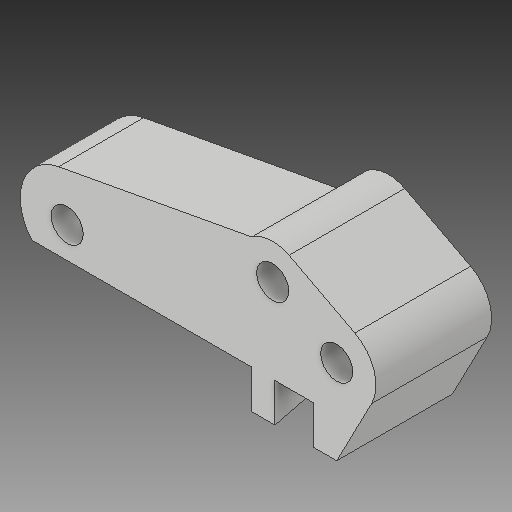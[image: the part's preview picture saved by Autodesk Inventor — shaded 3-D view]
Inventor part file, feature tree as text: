
AUTODESK INVENTOR PART (.ipt)
format: ipt  version: 2017 (Build 210142000, 142)  size: 423,936 bytes
history: native  units: mm
features: extrude x37, sketch x37, shell x1
ambient origin geometry x8: Origin, YZ Plane, XZ Plane, XY Plane, X Axis, Y Axis, Z Axis, Center Point
bodies: Solid1 (feature_tree)
feature tree (75):
  extrude  "Extrusion1"  Depth=37.0mm
  shell  "Shell1"  Thickness=20.0mm
  extrude  "Extrusion2"  Depth=11.0mm
  extrude  "Extrusion3"  TaperAngle=0.0deg  [1 undecoded]
  extrude  "Extrusion4"  Depth=5.0mm
  extrude  "Extrusion5"  TaperAngle=0.0deg  [1 undecoded]
  extrude  "Extrusion6"  Depth=10.0mm TaperAngle=0.0deg
  extrude  "Extrusion7"  Depth=15.0mm TaperAngle=0.0deg
  extrude  "Extrusion9"  Depth=8.5mm
  extrude  "Extrusion10"  Depth=15.0mm TaperAngle=0.0deg
  extrude  "Extrusion11"  Depth=35.46mm
  extrude  "Extrusion12"  Depth=15.0mm TaperAngle=0.0deg
  extrude  "Extrusion13"  Depth=4.5mm
  extrude  "Extrusion14"  Depth=15.0mm TaperAngle=0.0deg
  extrude  "Extrusion15"  Depth=8.5mm
  extrude  "Extrusion16"  Depth=15.0mm TaperAngle=0.0deg
  extrude  "Extrusion17"  Depth=28.505mm
  extrude  "Extrusion18"  Depth=15.0mm TaperAngle=0.0deg
  extrude  "Extrusion19"  Depth=36.0mm
  extrude  "Extrusion20"  Depth=15.0mm TaperAngle=0.0deg
  extrude  "Extrusion23"  Depth=5.0mm
  extrude  "Extrusion21"  Depth=4.1656mm
  extrude  "Extrusion22"  Depth=35.46mm
  extrude  "Extrusion24"  Depth=10.0mm
  extrude  "Extrusion25"  Depth=10.0mm TaperAngle=0.0deg
  extrude  "Extrusion26"  Depth=2.583mm TaperAngle=0.0deg
  extrude  "Extrusion27"  Depth=2.583mm TaperAngle=0.0deg
  extrude  "Extrusion28"  Depth=100.0mm TaperAngle=0.0deg
  extrude  "Extrusion29"  Depth=5.0mm
  extrude  "Extrusion30"  Depth=1.0mm
  extrude  "Extrusion31"  Depth=5.0mm
  extrude  "Extrusion32"  Depth=4.1656mm
  extrude  "Extrusion33"  Depth=6.161mm
  extrude  "Extrusion34"  Depth=4.1656mm
  extrude  "Extrusion35"  Depth=15.906mm
  extrude  "Extrusion36"  Depth=22.5mm TaperAngle=0.0deg
  extrude  "Extrusion37"  Depth=22.5mm TaperAngle=0.0deg
  extrude  "Extrusion38"  Depth=5.0mm
  sketch  "Sketch1"  dims[d0=35.0mm d1=37.0mm d2=20.0mm]
  sketch  "Sketch2"  dims[d3=11.0mm d4=55.0mm]
  sketch  "Sketch3"  dims[d5=26.0mm d6=0.0mm]
  sketch  "Sketch4"  dims[d7=50.0mm d8=0.0mm d9=5.0mm]
  sketch  "Sketch5"  dims[d10=17.0mm d11=0.0mm]
  sketch  "Sketch6"  dims[d12=11.0mm d13=10.0mm d14=0.0mm]
  sketch  "Sketch7"  dims[d15=15.0mm d16=0.0mm d17=15.0mm d18=0.0mm]
  sketch  "Sketch13"  dims[d19=4.1656mm d20=8.5mm]
  sketch  "Sketch14"  dims[d21=11.5mm d22=15.0mm d23=0.0mm]
  sketch  "Sketch15"  dims[d24=4.1656mm d25=35.46mm]
  sketch  "Sketch16"  dims[d26=23.505mm d27=15.0mm d28=0.0mm]
  sketch  "Sketch17"  dims[d29=4.1656mm d30=4.5mm]
  sketch  "Sketch18"  dims[d31=14.0mm d32=15.0mm d33=0.0mm]
  sketch  "Sketch20"  dims[d41=4.1656mm d42=8.5mm]
  sketch  "Sketch21"  dims[d43=11.5mm d44=15.0mm d45=0.0mm]
  sketch  "Sketch22"  dims[d46=4.1656mm d47=28.505mm]
  sketch  "Sketch23"  dims[d48=35.46mm d49=15.0mm d50=0.0mm]
  sketch  "Sketch24"  dims[d51=4.1656mm d52=36.0mm]
  sketch  "Sketch25"  dims[d53=4.5mm d54=15.0mm d55=0.0mm]
  sketch  "Sketch26"  dims[d56=5.0mm d57=50.0mm]
  sketch  "Sketch27"  dims[d58=21.0mm d59=0.0mm d60=4.1656mm]
  sketch  "Sketch28"  dims[d61=23.505mm d62=35.46mm]
  sketch  "Sketch29"  dims[d63=10.0mm d64=0.0mm d65=4.1656mm]
  sketch  "Sketch30"  dims[d67=36.0mm d68=10.0mm d69=0.0mm]
  sketch  "Sketch31"  dims[d70=4.5mm d71=2.583mm d72=0.0mm]
  sketch  "Sketch33"  dims[d73=2.583mm d74=0.0mm d75=2.583mm d76=0.0mm]
  sketch  "Sketch34"  dims[d77=6.917mm d78=100.0mm d79=0.0mm]
  sketch  "Sketch35"  dims[d80=5.0mm d81=5.0mm]
  sketch  "Sketch39"  dims[d83=1.0mm d84=1.0mm]
  sketch  "Sketch40"  dims[d85=100.0mm d86=0.0mm d87=5.0mm]
  sketch  "Sketch41"  dims[d88=22.5mm d89=0.0mm d90=4.1656mm]
  sketch  "Sketch42"  dims[d91=5.851mm d92=6.161mm]
  sketch  "Sketch43"  dims[d93=25.0mm d94=0.0mm d95=4.1656mm]
  sketch  "Sketch44"  dims[d96=2.702mm d97=15.906mm]
  sketch  "Sketch45"  dims[d98=25.0mm d99=0.0mm d100=22.5mm d101=0.0mm]
  sketch  "Sketch47"  dims[d102=2.5mm d103=22.5mm d104=0.0mm]
  sketch  "Sketch48"  dims[d105=9.0mm d106=5.0mm d107=5.0mm d108=0.0mm d109=30.0mm d110=0.0mm d111=4.1656mm d112=6.083mm d113=4.0mm d114=30.0mm d115=0.0mm d116=30.0mm d117=0.0mm d118=30.0mm d119=0.0mm d120=8.0mm d121=0.0mm d130=11.0mm d131=15.0mm d132=0.0mm d133=0.0mm d134=5.0mm d135=0.0mm d136=190.0mm d137=0.0mm d138=50.0mm d139=0.0mm d140=50.0mm d141=0.0mm d142=15.0mm d143=0.0mm d144=3.0mm d145=3.0mm d146=5.0mm d147=1.0mm d148=1.0mm d149=5.0mm d150=0.0mm d151=3.0mm d152=1.0mm d153=3.0mm d154=1.0mm d155=5.0mm d156=5.0mm d157=0.0mm d158=135.0deg d159=4.1656mm d160=15.0mm d161=0.0mm d162=3.0mm d163=15.0mm d164=0.0mm d165=4.1656mm d166=0.0mm d167=0.0mm d168=15.0mm d169=0.0mm]
note: 2 required parameter values undecoded (feature->parameter linkage not recoverable at this tier; creation-order binding heuristic only, values carry confidence <= 0.55)
